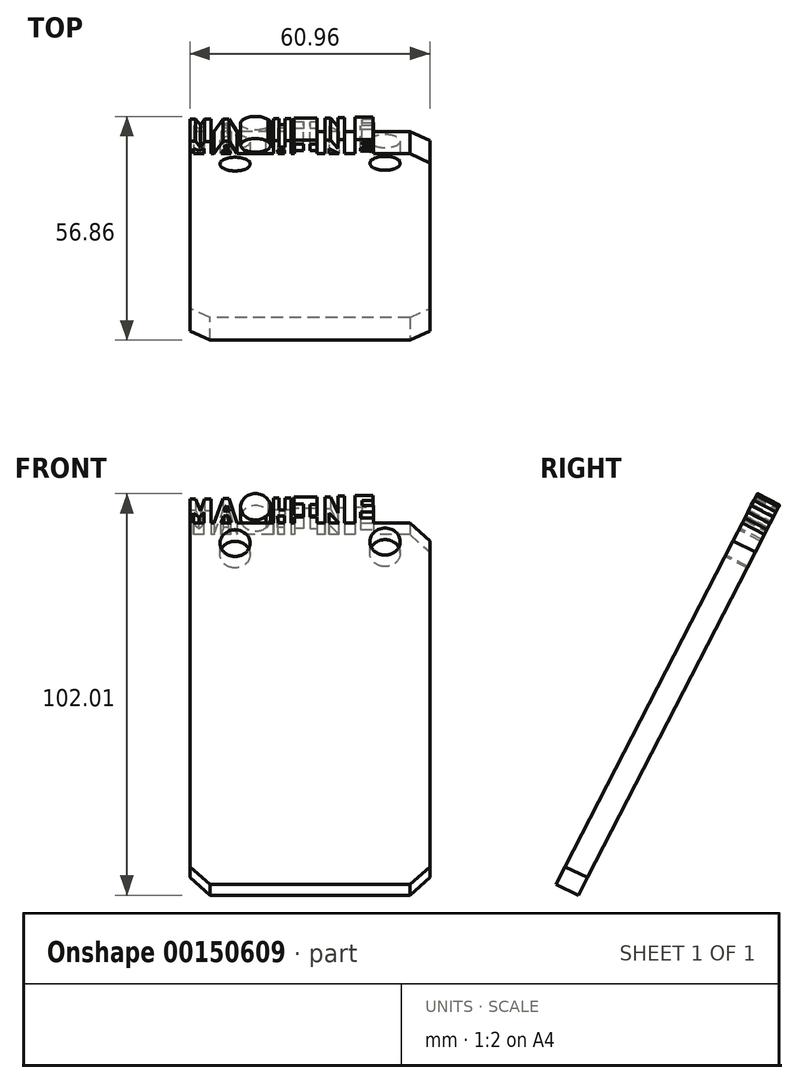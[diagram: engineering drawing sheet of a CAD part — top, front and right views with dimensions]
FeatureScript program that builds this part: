
annotation { "Feature Type Name" : "Feature", "Feature Type Description" : "" }
export const myFeature = defineFeature(function(context is Context, id is Id, definition is map)
    precondition{}
    {
        {
            var Q0;
            Q0=qCreatedBy(makeId("Right.planeOp"),FACE);
            var sketch = newSketch(context, id + "F0", { "sketchPlane" : qUnion([Q0])});
            skLineSegment(sketch, "E0", {"start": v(-1.16, 48.37) * mm, "end": v(-48.42, -43.28) * mm});
            skLineSegment(sketch, "E1", {"start": v(-1.16, 48.37) * mm, "end": v(-6.8, 51.28) * mm});
            skLineSegment(sketch, "E2", {"start": v(-6.8, 51.28) * mm, "end": v(-54.18, -40.6) * mm});
            skLineSegment(sketch, "E3", {"start": v(-48.42, -43.28) * mm, "end": v(-54.18, -40.6) * mm});
            skSolve(sketch);
        }
        {
            var Q0;
            Q0 = qSketchRegion(id + "F0", true);
            extrude(context, id + "F1", {"entities" : qUnion([Q0]), "depth" : 60.96 * mm});
        }
        {
            var Q0;
            Q0=makeQuery(id+"F1.opExtrude","SWEPT_FACE",FACE,{"disambiguationData":[OSD([sQuery(id+"F0.wireOp",EDGE,"E2")])]});
            var sketch = newSketch(context, id + "F2", { "sketchPlane" : qUnion([Q0])});
            skCircle(sketch, "E4", {"center": v(11.49, 36.7) * mm, "radius": 3.81 * mm});
            skCircle(sketch, "E5", {"center": v(49.59, 37.12) * mm, "radius": 3.85 * mm});
            skSolve(sketch);
        }
        {
            var Q0;
            Q0 = qSketchRegion(id + "F2", true);
            extrude(context, id + "F3", {"entities" : qUnion([Q0]), "operationType" : NewBodyOperationType.REMOVE, "oppositeDirection" : true, "depth" : 25.4 * mm});
        }
        {
            var Q0;
            Q0=makeQuery(id+"F1.opExtrude","SWEPT_FACE",FACE,{"disambiguationData":[OSD([sQuery(id+"F0.wireOp",EDGE,"E0")])]});
            var sketch = newSketch(context, id + "F4", { "sketchPlane" : qUnion([Q0])});
            skLineSegment(sketch, "E6", {"start": v(0, 42.46) * mm, "end": v(0, 49.38) * mm});
            skLineSegment(sketch, "E7", {"start": v(0, 49.38) * mm, "end": v(-1.42, 49.38) * mm});
            skLineSegment(sketch, "E8", {"start": v(-1.42, 49.38) * mm, "end": v(-2.7, 45.88) * mm});
            skLineSegment(sketch, "E9", {"start": v(-2.7, 45.88) * mm, "end": v(-3.77, 49.28) * mm});
            skLineSegment(sketch, "E10", {"start": v(-3.77, 49.28) * mm, "end": v(-5.32, 49.28) * mm});
            skLineSegment(sketch, "E11", {"start": v(-5.32, 49.28) * mm, "end": v(-5.32, 42.46) * mm});
            skLineSegment(sketch, "E12", {"start": v(-6.18, 42.46) * mm, "end": v(-8.4, 49.43) * mm});
            skLineSegment(sketch, "E13", {"start": v(-8.4, 49.43) * mm, "end": v(-9.95, 49.43) * mm});
            skLineSegment(sketch, "E14", {"start": v(-9.95, 49.43) * mm, "end": v(-11.94, 42.46) * mm});
            skArc(sketch, "E15", {"start": v(-19.32, 44.37) * mm, "mid": v(-12.92, 47.5) * mm, "end": v(-19.87, 49.08) * mm});
            skFitSpline(sketch, "E16", {"points": [v(-19.87, 49.08) * mm, v(-16.67, 47.07) * mm, v(-19.32, 44.37) * mm, v(-19.87, 49.08) * mm]});
            skLineSegment(sketch, "E17", {"start": v(-21.2, 42.46) * mm, "end": v(-21.2, 49.61) * mm});
            skLineSegment(sketch, "E18", {"start": v(-21.2, 49.61) * mm, "end": v(-22.7, 49.61) * mm});
            skLineSegment(sketch, "E19", {"start": v(-22.7, 49.61) * mm, "end": v(-22.7, 46.19) * mm});
            skLineSegment(sketch, "E20", {"start": v(-22.7, 46.19) * mm, "end": v(-24.14, 46.19) * mm});
            skLineSegment(sketch, "E21", {"start": v(-24.14, 46.19) * mm, "end": v(-24.14, 49.6) * mm});
            skLineSegment(sketch, "E22", {"start": v(-24.14, 49.6) * mm, "end": v(-25.7, 49.6) * mm});
            skLineSegment(sketch, "E23", {"start": v(-25.7, 49.6) * mm, "end": v(-25.7, 41.7) * mm});
            skLineSegment(sketch, "E24", {"start": v(-29.02, 49.9) * mm, "end": v(-26.43, 49.9) * mm});
            skLineSegment(sketch, "E25", {"start": v(-26.43, 49.9) * mm, "end": v(-26.43, 47.88) * mm});
            skLineSegment(sketch, "E26", {"start": v(-26.43, 47.88) * mm, "end": v(-28.85, 47.88) * mm});
            skLineSegment(sketch, "E27", {"start": v(-28.85, 47.88) * mm, "end": v(-28.85, 44.13) * mm});
            skLineSegment(sketch, "E28", {"start": v(-28.85, 44.13) * mm, "end": v(-26.64, 44.13) * mm});
            skLineSegment(sketch, "E29", {"start": v(-26.64, 44.13) * mm, "end": v(-26.64, 42.46) * mm});
            skLineSegment(sketch, "E30", {"start": v(-29.02, 49.9) * mm, "end": v(-32.35, 49.9) * mm});
            skLineSegment(sketch, "E31", {"start": v(-32.35, 49.9) * mm, "end": v(-32.35, 47.77) * mm});
            skLineSegment(sketch, "E32", {"start": v(-32.35, 47.77) * mm, "end": v(-30.48, 47.77) * mm});
            skLineSegment(sketch, "E33", {"start": v(-30.48, 47.77) * mm, "end": v(-30.48, 44.2) * mm});
            skLineSegment(sketch, "E34", {"start": v(-30.48, 44.2) * mm, "end": v(-32.25, 44.2) * mm});
            skLineSegment(sketch, "E35", {"start": v(-32.25, 44.2) * mm, "end": v(-32.25, 42.46) * mm});
            skLineSegment(sketch, "E36", {"start": v(-34.35, 42.46) * mm, "end": v(-34.35, 49.9) * mm});
            skLineSegment(sketch, "E37", {"start": v(-34.35, 49.9) * mm, "end": v(-35.68, 49.9) * mm});
            skLineSegment(sketch, "E38", {"start": v(-35.68, 49.9) * mm, "end": v(-37.6, 45.3) * mm});
            skLineSegment(sketch, "E39", {"start": v(-37.6, 45.3) * mm, "end": v(-37.6, 50.18) * mm});
            skLineSegment(sketch, "E40", {"start": v(-37.6, 50.18) * mm, "end": v(-39.26, 50.18) * mm});
            skLineSegment(sketch, "E41", {"start": v(-39.26, 50.18) * mm, "end": v(-39.26, 42.46) * mm});
            skLineSegment(sketch, "E42", {"start": v(-41.94, 50.32) * mm, "end": v(-41.94, 42.46) * mm});
            skLineSegment(sketch, "E43", {"start": v(-41.94, 50.32) * mm, "end": v(-46.57, 50.32) * mm});
            skLineSegment(sketch, "E44", {"start": v(-46.57, 50.32) * mm, "end": v(-46.57, 48.92) * mm});
            skLineSegment(sketch, "E45", {"start": v(-46.57, 48.92) * mm, "end": v(-43.71, 48.92) * mm});
            skLineSegment(sketch, "E46", {"start": v(-43.71, 48.92) * mm, "end": v(-43.71, 47.4) * mm});
            skLineSegment(sketch, "E47", {"start": v(-43.71, 47.4) * mm, "end": v(-46.63, 47.4) * mm});
            skLineSegment(sketch, "E48", {"start": v(-46.63, 47.4) * mm, "end": v(-46.63, 45.6) * mm});
            skLineSegment(sketch, "E49", {"start": v(-46.63, 45.6) * mm, "end": v(-43.3, 45.6) * mm});
            skLineSegment(sketch, "E50", {"start": v(-43.3, 45.6) * mm, "end": v(-43.3, 43.9) * mm});
            skLineSegment(sketch, "E51", {"start": v(-43.3, 43.9) * mm, "end": v(-46.61, 43.9) * mm});
            skLineSegment(sketch, "E52", {"start": v(-46.61, 43.9) * mm, "end": v(-46.61, 42.46) * mm});
            skLineSegment(sketch, "E53", {"start": v(-46.61, 42.46) * mm, "end": v(0, 42.46) * mm});
            skSolve(sketch);
        }
        {
            var Q0;
            Q0 = qSketchRegion(id + "F4", true);
            extrude(context, id + "F5", {"entities" : qUnion([Q0]), "operationType" : NewBodyOperationType.ADD, "oppositeDirection" : true, "depth" : 6.35 * mm});
        }
        {
            var Q0;
            {var subQ0=sQuery(id+"F4.wireOp",EDGE,"E53");Q0=makeQuery(id+"F5.boolean.opBoolean","MERGE",FACE,{"derivedFrom":[makeQuery(id+"F1.opExtrude","SWEPT_FACE",FACE,{"disambiguationData":[OSD([sQuery(id+"F0.wireOp",EDGE,"E2")])]}),makeQuery(id+"F5.opExtrude","CAP_FACE",FACE,{"disambiguationData":[OSD([sQuery(id+"F4.wireOp",EDGE,"E6"),sQuery(id+"F4.wireOp",EDGE,"E7"),sQuery(id+"F4.wireOp",EDGE,"E8"),sQuery(id+"F4.wireOp",EDGE,"E9"),sQuery(id+"F4.wireOp",EDGE,"E10"),sQuery(id+"F4.wireOp",EDGE,"E11"),subQ0])],"isStart":false}),makeQuery(id+"F5.opExtrude","CAP_FACE",FACE,{"disambiguationData":[OSD([sQuery(id+"F4.wireOp",EDGE,"E12"),sQuery(id+"F4.wireOp",EDGE,"E13"),sQuery(id+"F4.wireOp",EDGE,"E14"),subQ0])],"isStart":false}),makeQuery(id+"F5.opExtrude","CAP_FACE",FACE,{"disambiguationData":[OSD([sQuery(id+"F4.wireOp",EDGE,"E17"),sQuery(id+"F4.wireOp",EDGE,"E18"),sQuery(id+"F4.wireOp",EDGE,"E19"),sQuery(id+"F4.wireOp",EDGE,"E20"),sQuery(id+"F4.wireOp",EDGE,"E21"),sQuery(id+"F4.wireOp",EDGE,"E22"),sQuery(id+"F4.wireOp",EDGE,"E23"),subQ0])],"isStart":false}),makeQuery(id+"F5.opExtrude","CAP_FACE",FACE,{"disambiguationData":[OSD([sQuery(id+"F4.wireOp",EDGE,"E24"),sQuery(id+"F4.wireOp",EDGE,"E25"),sQuery(id+"F4.wireOp",EDGE,"E26"),sQuery(id+"F4.wireOp",EDGE,"E27"),sQuery(id+"F4.wireOp",EDGE,"E28"),sQuery(id+"F4.wireOp",EDGE,"E29"),sQuery(id+"F4.wireOp",EDGE,"E30"),sQuery(id+"F4.wireOp",EDGE,"E31"),sQuery(id+"F4.wireOp",EDGE,"E32"),sQuery(id+"F4.wireOp",EDGE,"E33"),sQuery(id+"F4.wireOp",EDGE,"E34"),sQuery(id+"F4.wireOp",EDGE,"E35"),subQ0])],"isStart":false}),makeQuery(id+"F5.opExtrude","CAP_FACE",FACE,{"disambiguationData":[OSD([sQuery(id+"F4.wireOp",EDGE,"E36"),sQuery(id+"F4.wireOp",EDGE,"E37"),sQuery(id+"F4.wireOp",EDGE,"E38"),sQuery(id+"F4.wireOp",EDGE,"E39"),sQuery(id+"F4.wireOp",EDGE,"E40"),sQuery(id+"F4.wireOp",EDGE,"E41"),subQ0])],"isStart":false}),makeQuery(id+"F5.opExtrude","CAP_FACE",FACE,{"disambiguationData":[OSD([sQuery(id+"F4.wireOp",EDGE,"E42"),sQuery(id+"F4.wireOp",EDGE,"E43"),sQuery(id+"F4.wireOp",EDGE,"E44"),sQuery(id+"F4.wireOp",EDGE,"E45"),sQuery(id+"F4.wireOp",EDGE,"E46"),sQuery(id+"F4.wireOp",EDGE,"E47"),sQuery(id+"F4.wireOp",EDGE,"E48"),sQuery(id+"F4.wireOp",EDGE,"E49"),sQuery(id+"F4.wireOp",EDGE,"E50"),sQuery(id+"F4.wireOp",EDGE,"E51"),sQuery(id+"F4.wireOp",EDGE,"E52"),subQ0])],"isStart":false})]});}
            var sketch = newSketch(context, id + "F6", { "sketchPlane" : qUnion([Q0])});
            skLineSegment(sketch, "E54", {"start": v(0, 42.43) * mm, "end": v(46.61, 42.46) * mm});
            skLineSegment(sketch, "E55", {"start": v(1, 42.43) * mm, "end": v(0.99, 45.35) * mm});
            skLineSegment(sketch, "E56", {"start": v(0.99, 45.35) * mm, "end": v(2.34, 44.05) * mm});
            skLineSegment(sketch, "E57", {"start": v(2.34, 44.05) * mm, "end": v(3.62, 45.39) * mm});
            skLineSegment(sketch, "E58", {"start": v(3.62, 45.39) * mm, "end": v(3.62, 42.44) * mm});
            skLineSegment(sketch, "E59", {"start": v(7.87, 42.44) * mm, "end": v(8.51, 44.4) * mm});
            skLineSegment(sketch, "E60", {"start": v(8.51, 44.4) * mm, "end": v(9.87, 44.4) * mm});
            skLineSegment(sketch, "E61", {"start": v(9.87, 44.4) * mm, "end": v(10.52, 42.44) * mm});
            skPoint(sketch, "E62.startSnap0", {"position": v(10.94, 45.94) * mm});
            skLineSegment(sketch, "E63", {"start": v(9.44, 47.47) * mm, "end": v(8.52, 45.94) * mm});
            skLineSegment(sketch, "E64", {"start": v(22.34, 42.45) * mm, "end": v(22.33, 44.4) * mm});
            skLineSegment(sketch, "E65", {"start": v(22.33, 44.4) * mm, "end": v(24.05, 44.4) * mm});
            skLineSegment(sketch, "E66", {"start": v(24.05, 44.4) * mm, "end": v(24.05, 42.45) * mm});
            skLineSegment(sketch, "E67", {"start": v(35.4, 42.46) * mm, "end": v(35.4, 45.33) * mm});
            skLineSegment(sketch, "E68", {"start": v(35.4, 45.33) * mm, "end": v(37.87, 42.46) * mm});
            skLineSegment(sketch, "E69", {"start": v(9.44, 47.47) * mm, "end": v(10.14, 45.76) * mm});
            skLineSegment(sketch, "E70", {"start": v(10.14, 45.76) * mm, "end": v(8.52, 45.94) * mm});
            skSolve(sketch);
        }
        {
            var Q0;
            Q0 = qSketchRegion(id + "F6", true);
            extrude(context, id + "F7", {"entities" : qUnion([Q0]), "operationType" : NewBodyOperationType.REMOVE, "oppositeDirection" : true, "depth" : 25.4 * mm});
        }
        {
            var Q0;
            Q0=makeQuery(id+"F1.opExtrude","CAP_EDGE",EDGE,{"disambiguationData":[OSD([sQuery(id+"F0.wireOp",EDGE,"E1")])],"isStart":false});
            var Q1;
            Q1=makeQuery(id+"F1.opExtrude","CAP_EDGE",EDGE,{"disambiguationData":[OSD([sQuery(id+"F0.wireOp",EDGE,"E3")])],"isStart":false});
            var Q2;
            Q2=makeQuery(id+"F1.opExtrude","CAP_EDGE",EDGE,{"disambiguationData":[OSD([sQuery(id+"F0.wireOp",EDGE,"E3")])],"isStart":true});
            chamfer(context, id + "F8", {"entities" : qUnion([Q0, Q1, Q2]), "width" : 5.08 * mm, "tangentPropagation" : true});
        }
    });
